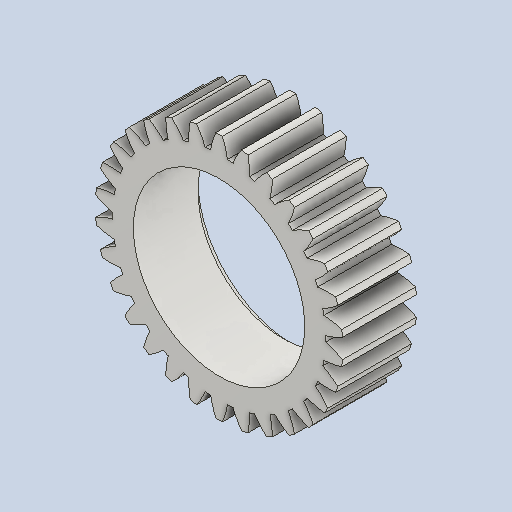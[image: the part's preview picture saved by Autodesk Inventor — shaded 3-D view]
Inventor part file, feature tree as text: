
AUTODESK INVENTOR PART (.ipt)
format: ipt  version: 2022 (Build 260153000, 153)  size: 344,576 bytes
history: native  units: in
note: dims shown in document units (in); Inventor stores cm internally (conversion verified against a paired STEP export)
features: other x12, plane x4, sketch x3
ambient origin geometry x8: Origin, YZ Plane, XZ Plane, XY Plane, X Axis, Y Axis, Z Axis, Center Point
bodies: Solid1 (feature_tree)
feature tree (19):
  other  "Spur Gear1"
  other  "Solid1::Spur Gear1"
  other  "TaggingFeature1"
  sketch  "Sketch1"  dims[d0=0.3937in]
  sketch  "Sketch2"  dims[d9=0.0in d14=0.0in d15=1.0in d16=0.0in d17=0.0in d18=0.0in d19=1.0in]
  sketch  "Sketch3"
  plane  "XZ Plane_1"
  plane  "Work Plane2"
  plane  "Work Plane3"
  plane  "Work Plane4"
  other  "Srf1"
  other  "Srf1::Derived"
  other  "Start plane iMate"
  other  "Distance iMate"
  other  "Position iMate"
  other  "Mesh iMate"
  other  "Axis iMate"
  other  "Mesh iMate2"
  other  "Align iMate"
